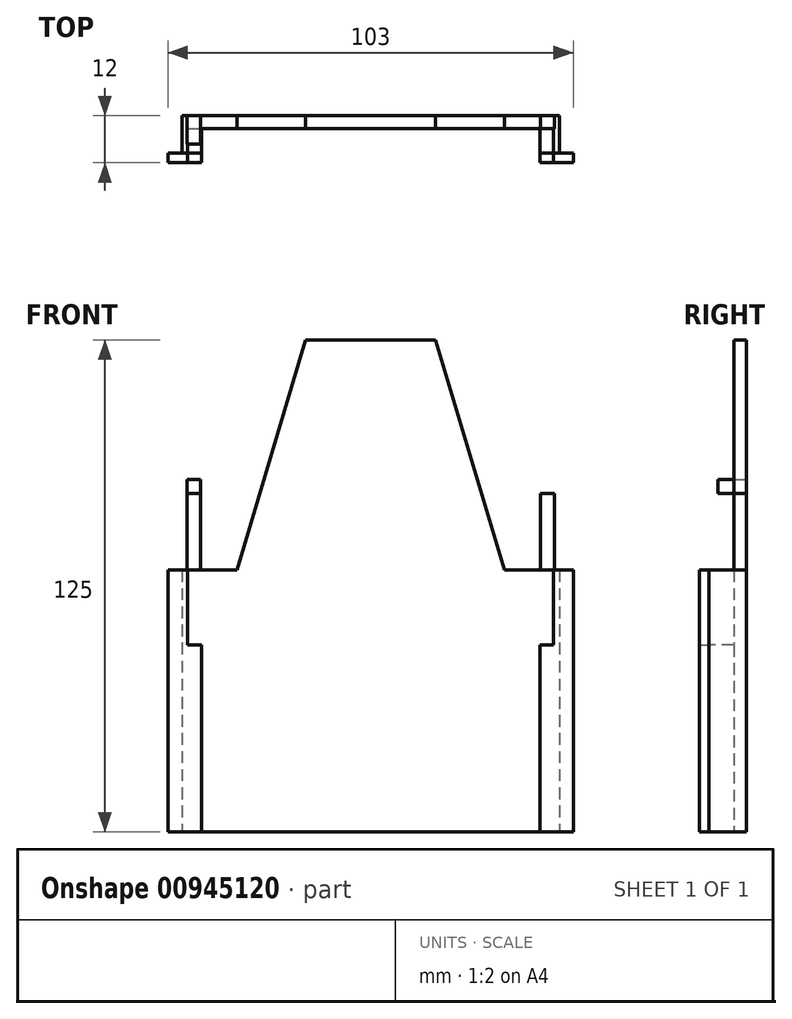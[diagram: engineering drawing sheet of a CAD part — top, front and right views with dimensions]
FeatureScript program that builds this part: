
annotation { "Feature Type Name" : "Feature", "Feature Type Description" : "" }
export const myFeature = defineFeature(function(context is Context, id is Id, definition is map)
    precondition{}
    {
        {
            var Q0;
            Q0=qCreatedBy(makeId("Front.planeOp"),FACE);
            var sketch = newSketch(context, id + "F0", { "sketchPlane" : qUnion([Q0])});
            skLineSegment(sketch, "E0.bottom", {"start": v(-25.95, 21.71) * mm, "end": v(77.05, 21.71) * mm});
            skLineSegment(sketch, "E0.top", {"start": v(-25.95, -44.79) * mm, "end": v(77.05, -44.79) * mm});
            skLineSegment(sketch, "E0.left", {"start": v(-25.95, 21.71) * mm, "end": v(-25.95, -44.79) * mm});
            skLineSegment(sketch, "E0.right", {"start": v(77.05, 21.71) * mm, "end": v(77.05, -44.79) * mm});
            skLineSegment(sketch, "E1", {"start": v(-25.95, 21.71) * mm, "end": v(-22.36, 21.71) * mm});
            skLineSegment(sketch, "E2", {"start": v(-22.36, 21.71) * mm, "end": v(-22.36, -44.79) * mm});
            skLineSegment(sketch, "E3", {"start": v(25.55, 21.71) * mm, "end": v(25.55, -44.79) * mm});
            skLineSegment(sketch, "E4", {"start": v(25.55, 21.71) * mm, "end": v(-17.45, 21.71) * mm});
            skLineSegment(sketch, "E5", {"start": v(-17.45, 21.71) * mm, "end": v(-17.45, -44.79) * mm});
            skLineSegment(sketch, "E6", {"start": v(-17.45, 21.71) * mm, "end": v(-20.95, 21.71) * mm});
            skLineSegment(sketch, "E7", {"start": v(-20.95, 21.71) * mm, "end": v(-20.95, 2.71) * mm});
            skLineSegment(sketch, "E8", {"start": v(-20.95, 2.71) * mm, "end": v(-17.45, 2.71) * mm});
            skLineSegment(sketch, "E9.MirrorCS", {"start": v(68.55, 21.71) * mm, "end": v(68.55, -44.79) * mm});
            skLineSegment(sketch, "E10.MirrorCS", {"start": v(72.05, 2.71) * mm, "end": v(68.55, 2.71) * mm});
            skLineSegment(sketch, "E11.MirrorCS", {"start": v(72.05, 21.71) * mm, "end": v(72.05, 2.71) * mm});
            skLineSegment(sketch, "E12.MirrorCS", {"start": v(68.55, 21.71) * mm, "end": v(72.05, 21.71) * mm});
            skLineSegment(sketch, "E13.MirrorCS", {"start": v(73.47, 21.71) * mm, "end": v(73.47, -44.79) * mm});
            skSolve(sketch);
        }
        {
            var Q0;
            {var subQ0=sQuery(id+"F0.wireOp",EDGE,"E0.left");Q0=makeQuery(id+"F0.imprint","IMPRINT",FACE,{"disambiguationData":[TD([[makeQuery(id+"F0.imprint","IMPRINT",EDGE,{"derivedFrom":subQ0}),1.0]])]});}
            var Q1;
            {var subQ0=sQuery(id+"F0.wireOp",EDGE,"E0.right");Q1=makeQuery(id+"F0.imprint","IMPRINT",FACE,{"disambiguationData":[TD([[makeQuery(id+"F0.imprint","IMPRINT",EDGE,{"derivedFrom":subQ0}),-1.0]])]});}
            var Q2;
            {var subQ4=sQuery(id+"F0.wireOp",EDGE,"E2");Q2=makeQuery(id+"F0.imprint","IMPRINT",FACE,{"disambiguationData":[TD([[makeQuery(id+"F0.imprint","IMPRINT",EDGE,{"derivedFrom":subQ4}),1.0]])]});}
            var Q3;
            {var subQ0=sQuery(id+"F0.wireOp",EDGE,"E10.MirrorCS");Q3=makeQuery(id+"F0.imprint","IMPRINT",FACE,{"disambiguationData":[TD([[makeQuery(id+"F0.imprint","IMPRINT",EDGE,{"derivedFrom":subQ0}),1.0]])]});}
            extrude(context, id + "F1", {"entities" : qUnion([Q0, Q1, Q2, Q3]), "depth" : 2.5 * mm, "offsetDistance" : 25 * mm});
        }
        {
            var Q0;
            {var subQ4=sQuery(id+"F0.wireOp",EDGE,"E2");Q0=makeQuery(id+"F0.imprint","IMPRINT",FACE,{"disambiguationData":[TD([[makeQuery(id+"F0.imprint","IMPRINT",EDGE,{"derivedFrom":subQ4}),1.0]])]});}
            var Q1;
            {var subQ0=sQuery(id+"F0.wireOp",EDGE,"E10.MirrorCS");Q1=makeQuery(id+"F0.imprint","IMPRINT",FACE,{"disambiguationData":[TD([[makeQuery(id+"F0.imprint","IMPRINT",EDGE,{"derivedFrom":subQ0}),1.0]])]});}
            extrude(context, id + "F2", {"entities" : qUnion([Q0, Q1]), "oppositeDirection" : true, "depth" : 9.5 * mm, "offsetDistance" : 25 * mm});
        }
        {
            var Q0;
            Q0=makeQuery(id+"F2.opExtrude","CAP_FACE",FACE,{"disambiguationData":[OSD([sQuery(id+"F0.wireOp",EDGE,"E0.bottom"),sQuery(id+"F0.wireOp",EDGE,"E0.top"),sQuery(id+"F0.wireOp",EDGE,"E2"),sQuery(id+"F0.wireOp",EDGE,"E5"),sQuery(id+"F0.wireOp",EDGE,"E7"),sQuery(id+"F0.wireOp",EDGE,"E8")])],"isStart":false});
            var sketch = newSketch(context, id + "F3", { "sketchPlane" : qUnion([Q0])});
            skLineSegment(sketch, "E14.left", {"start": v(22.36, 21.71) * mm, "end": v(22.36, -44.79) * mm});
            skLineSegment(sketch, "E15", {"start": v(22.36, 21.71) * mm, "end": v(-73.47, 21.71) * mm});
            skLineSegment(sketch, "E16", {"start": v(-73.47, 21.71) * mm, "end": v(-73.47, -44.79) * mm});
            skLineSegment(sketch, "E17", {"start": v(-73.47, -44.79) * mm, "end": v(22.36, -44.79) * mm});
            skLineSegment(sketch, "E18", {"start": v(-25.55, -44.79) * mm, "end": v(-25.55, 80.21) * mm});
            skLineSegment(sketch, "E19", {"start": v(-25.55, 80.21) * mm, "end": v(-42.05, 80.21) * mm});
            skLineSegment(sketch, "E20", {"start": v(-25.55, 21.71) * mm, "end": v(-59.55, 21.71) * mm});
            skLineSegment(sketch, "E21", {"start": v(-59.55, 21.71) * mm, "end": v(-42.05, 80.21) * mm});
            skLineSegment(sketch, "E22.MirrorCS", {"start": v(8.45, 21.71) * mm, "end": v(-9.05, 80.21) * mm});
            skLineSegment(sketch, "E23.MirrorCS", {"start": v(-25.55, 80.21) * mm, "end": v(-9.05, 80.21) * mm});
            skSolve(sketch);
        }
        {
            var Q0;
            {var subQ5=makeQuery(id+"F2.opExtrude","CAP_EDGE",EDGE,{"disambiguationData":[OSD([sQuery(id+"F0.wireOp",EDGE,"E5")])],"isStart":false});Q0=makeQuery(id+"F3.imprint","IMPRINT",FACE,{"disambiguationData":[TD([[makeQuery(id+"F3.imprint","IMPRINT",EDGE,{"derivedFrom":subQ5}),-1.0]])]});}
            var Q1;
            {var subQ3=sQuery(id+"F3.wireOp",EDGE,"E22.MirrorCS");Q1=makeQuery(id+"F3.imprint","IMPRINT",FACE,{"disambiguationData":[TD([[makeQuery(id+"F3.imprint","IMPRINT",EDGE,{"derivedFrom":subQ3}),1.0]])]});}
            var Q2;
            {var subQ0=sQuery(id+"F3.wireOp",EDGE,"E19");Q2=makeQuery(id+"F3.imprint","IMPRINT",FACE,{"disambiguationData":[TD([[makeQuery(id+"F3.imprint","IMPRINT",EDGE,{"derivedFrom":subQ0}),1.0]])]});}
            var Q3;
            {var subQ1=sQuery(id+"F3.wireOp",EDGE,"E16");Q3=makeQuery(id+"F3.imprint","IMPRINT",FACE,{"disambiguationData":[TD([[makeQuery(id+"F3.imprint","IMPRINT",EDGE,{"derivedFrom":subQ1}),1.0]])]});}
            var Q4;
            Q4 = qSketchRegion(id + "FRfURfbXSc61GAG_6", true);
            extrude(context, id + "F4", {"entities" : qUnion([Q0, Q1, Q2, Q3, Q4]), "operationType" : NewBodyOperationType.ADD, "oppositeDirection" : true, "depth" : 3.25 * mm, "offsetDistance" : 25 * mm});
        }
        {
            var Q0;
            {var subQ1=sQuery(id+"F3.wireOp",EDGE,"E16");Q0=makeQuery(id+"F3.imprint","IMPRINT",FACE,{"disambiguationData":[TD([[makeQuery(id+"F3.imprint","IMPRINT",EDGE,{"derivedFrom":subQ1}),1.0]])]});}
            var sketch = newSketch(context, id + "F5", { "sketchPlane" : qUnion([Q0])});
            skLineSegment(sketch, "E24.bottom", {"start": v(-72.24, 21.71) * mm, "end": v(-68.74, 21.71) * mm});
            skLineSegment(sketch, "E24.top", {"start": v(-72.24, 41.21) * mm, "end": v(-68.74, 41.21) * mm});
            skLineSegment(sketch, "E24.left", {"start": v(-72.24, 21.71) * mm, "end": v(-72.24, 41.21) * mm});
            skLineSegment(sketch, "E24.right", {"start": v(-68.74, 21.71) * mm, "end": v(-68.74, 41.21) * mm});
            skLineSegment(sketch, "E25.bottom", {"start": v(-68.74, 41.21) * mm, "end": v(-72.24, 41.21) * mm});
            skLineSegment(sketch, "E25.top", {"start": v(-68.74, 44.71) * mm, "end": v(-72.24, 44.71) * mm});
            skLineSegment(sketch, "E25.left", {"start": v(-68.74, 41.21) * mm, "end": v(-68.74, 44.71) * mm});
            skLineSegment(sketch, "E25.right", {"start": v(-72.24, 41.21) * mm, "end": v(-72.24, 44.71) * mm});
            skLineSegment(sketch, "E26.MirrorCS", {"start": v(17.63, 21.71) * mm, "end": v(17.63, 41.21) * mm});
            skLineSegment(sketch, "E27.MirrorCS", {"start": v(21.13, 21.71) * mm, "end": v(21.13, 41.21) * mm});
            skLineSegment(sketch, "E28.MirrorCS", {"start": v(21.13, 21.71) * mm, "end": v(17.63, 21.71) * mm});
            skLineSegment(sketch, "E29.MirrorCS", {"start": v(17.63, 41.21) * mm, "end": v(21.13, 41.21) * mm});
            skLineSegment(sketch, "E30.MirrorCS", {"start": v(17.63, 44.71) * mm, "end": v(21.13, 44.71) * mm});
            skLineSegment(sketch, "E31.MirrorCS", {"start": v(17.63, 41.21) * mm, "end": v(17.63, 44.71) * mm});
            skLineSegment(sketch, "E32.MirrorCS", {"start": v(21.13, 41.21) * mm, "end": v(21.13, 44.71) * mm});
            skSolve(sketch);
        }
        {
            var Q0;
            Q0=makeQuery(id+"F5.imprint","IMPRINT",FACE,{"disambiguationData":[TD([[makeQuery(id+"F5.imprint","IMPRINT",EDGE,{"derivedFrom":sQuery(id+"F5.wireOp",EDGE,"E24.bottom")}),1.0]])]});
            var Q1;
            Q1=makeQuery(id+"F5.imprint","IMPRINT",FACE,{"disambiguationData":[TD([[makeQuery(id+"F5.imprint","IMPRINT",EDGE,{"derivedFrom":sQuery(id+"F5.wireOp",EDGE,"E26.MirrorCS")}),-1.0]])]});
            extrude(context, id + "F6", {"entities" : qUnion([Q0, Q1]), "oppositeDirection" : true, "depth" : 3.25 * mm, "offsetDistance" : 25 * mm});
        }
        {
            var Q0;
            Q0=makeQuery(id+"F5.imprint","IMPRINT",FACE,{"disambiguationData":[TD([[makeQuery(id+"F5.imprint","IMPRINT",EDGE,{"derivedFrom":sQuery(id+"F5.wireOp",EDGE,"E25.bottom")}),-1.0]])]});
            var Q1;
            Q1=makeQuery(id+"F5.imprint","IMPRINT",FACE,{"disambiguationData":[TD([[makeQuery(id+"F5.imprint","IMPRINT",EDGE,{"derivedFrom":sQuery(id+"F5.wireOp",EDGE,"E29.MirrorCS")}),1.0]])]});
            extrude(context, id + "F7", {"entities" : qUnion([Q0, Q1]), "oppositeDirection" : true, "depth" : 7.25 * mm, "offsetDistance" : 25 * mm});
        }
    });
